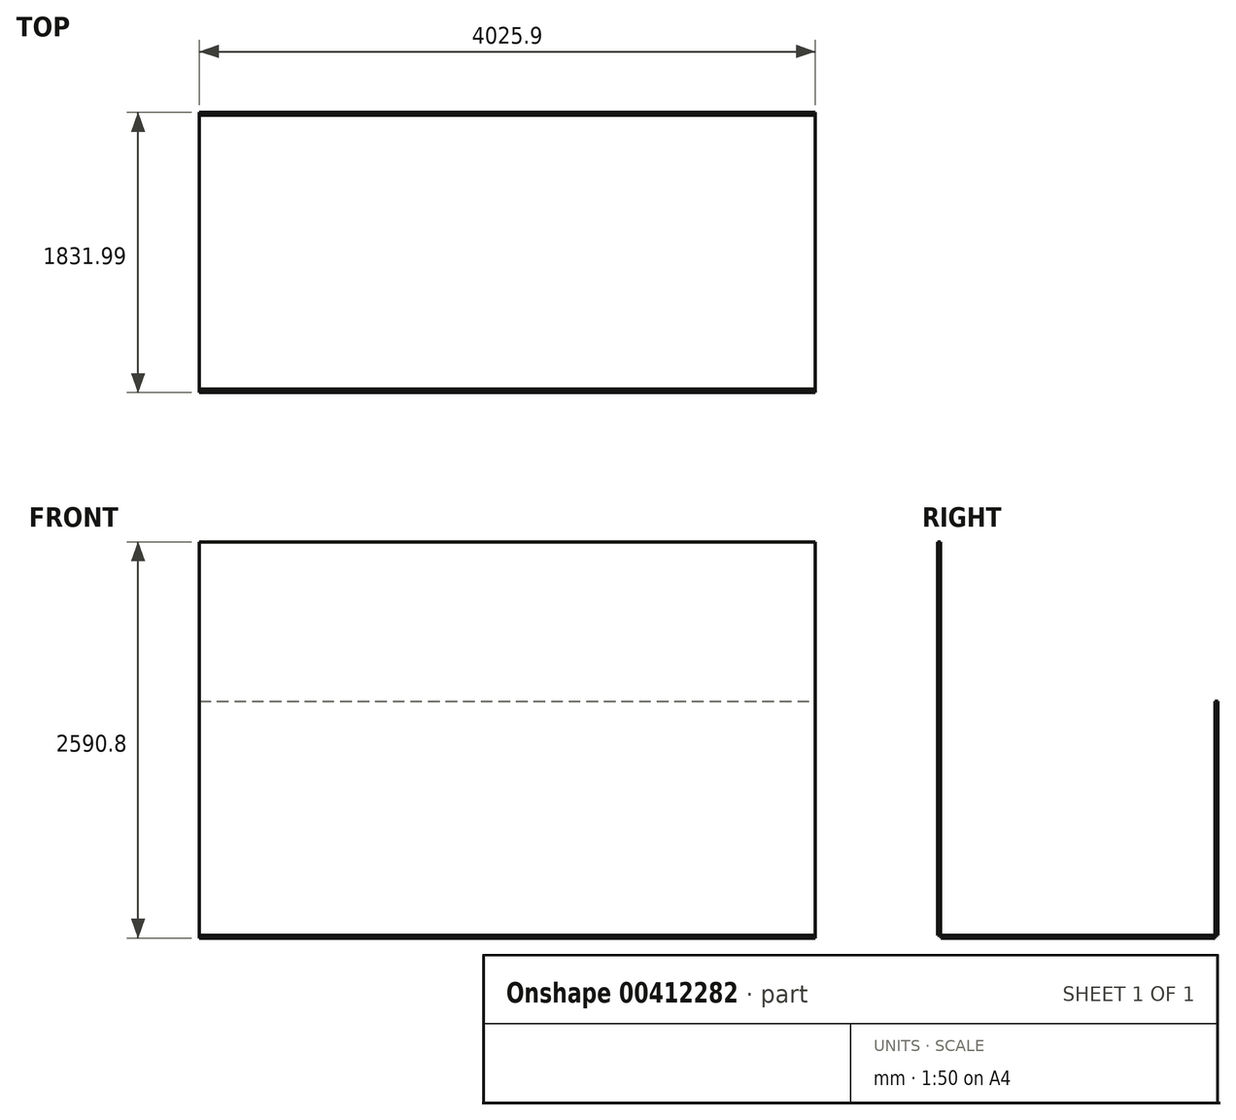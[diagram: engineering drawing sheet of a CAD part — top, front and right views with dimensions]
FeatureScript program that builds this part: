
annotation { "Feature Type Name" : "Feature", "Feature Type Description" : "" }
export const myFeature = defineFeature(function(context is Context, id is Id, definition is map)
    precondition{}
    {
        {
            var Q0;
            Q0=qCreatedBy(makeId("Top.planeOp"),FACE);
            var sketch = newSketch(context, id + "F0", { "sketchPlane" : qUnion([Q0])});
            skPoint(sketch, "E0.middle", {"position": v(0, 0) * mm});
            skLineSegment(sketch, "E1.bottom", {"start": v(0, 0) * mm, "end": v(4025.9, 0) * mm});
            skLineSegment(sketch, "E1.top", {"start": v(0, -1790.7) * mm, "end": v(4025.9, -1790.7) * mm});
            skLineSegment(sketch, "E1.left", {"start": v(0, 0) * mm, "end": v(0, -1790.7) * mm});
            skLineSegment(sketch, "E1.right", {"start": v(4025.9, 0) * mm, "end": v(4025.9, -1790.7) * mm});
            skSolve(sketch);
        }
        {
            var Q0;
            Q0=makeQuery(id+"F0.imprint","IMPRINT",FACE,{"disambiguationData":[TD([[makeQuery(id+"F0.imprint","IMPRINT",EDGE,{"derivedFrom":sQuery(id+"F0.wireOp",EDGE,"E0.bottom")}),-1.0]])]});
            var Q1;
            Q1=makeQuery(id+"F0.imprint","IMPRINT",FACE,{"disambiguationData":[TD([[makeQuery(id+"F0.imprint","IMPRINT",EDGE,{"derivedFrom":sQuery(id+"F0.wireOp",EDGE,"E1.bottom")}),-1.0]])]});
            extrude(context, id + "F1", {"entities" : qUnion([Q0, Q1]), "depth" : -19.05 * mm});
        }
        {
            var Q0;
            Q0=qCreatedBy(makeId("Front.planeOp"),FACE);
            var sketch = newSketch(context, id + "F2", { "sketchPlane" : qUnion([Q0])});
            skLineSegment(sketch, "E2.bottom", {"start": v(0, 0) * mm, "end": v(4025.9, 0) * mm});
            skLineSegment(sketch, "E2.top", {"start": v(0, 1530.35) * mm, "end": v(4025.9, 1530.35) * mm});
            skLineSegment(sketch, "E2.left", {"start": v(0, 0) * mm, "end": v(0, 1530.35) * mm});
            skLineSegment(sketch, "E2.right", {"start": v(4025.9, 0) * mm, "end": v(4025.9, 1530.35) * mm});
            skSolve(sketch);
        }
        {
            var Q0;
            Q0=makeQuery(id+"F2.imprint","IMPRINT",FACE,{"disambiguationData":[TD([[makeQuery(id+"F2.imprint","IMPRINT",EDGE,{"derivedFrom":sQuery(id+"F2.wireOp",EDGE,"E2.bottom")}),1.0]])]});
            extrude(context, id + "F3", {"entities" : qUnion([Q0]), "oppositeDirection" : true, "depth" : 19.05 * mm});
        }
        {
            var Q0;
            Q0=qCreatedBy(makeId("Right.planeOp"),FACE);
            var sketch = newSketch(context, id + "F4", { "sketchPlane" : qUnion([Q0])});
            skLineSegment(sketch, "E3.bottom", {"start": v(-1793.89, 0) * mm, "end": v(-1812.94, 0) * mm});
            skLineSegment(sketch, "E3.top", {"start": v(-1793.89, 2571.75) * mm, "end": v(-1812.94, 2571.75) * mm});
            skLineSegment(sketch, "E3.left", {"start": v(-1793.89, 0) * mm, "end": v(-1793.89, 2571.75) * mm});
            skLineSegment(sketch, "E3.right", {"start": v(-1812.94, 0) * mm, "end": v(-1812.94, 2571.75) * mm});
            skSolve(sketch);
        }
        {
            var Q0;
            Q0=makeQuery(id+"F4.imprint","IMPRINT",FACE,{"disambiguationData":[TD([[makeQuery(id+"F4.imprint","IMPRINT",EDGE,{"derivedFrom":sQuery(id+"F4.wireOp",EDGE,"E3.bottom")}),-1.0]])]});
            extrude(context, id + "F5", {"entities" : qUnion([Q0]), "depth" : 4025.9 * mm});
        }
    });
